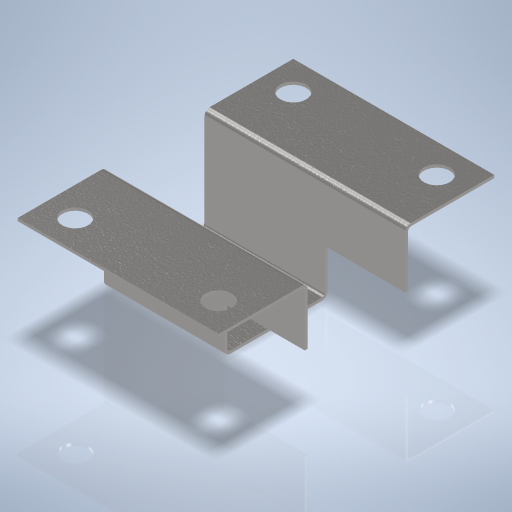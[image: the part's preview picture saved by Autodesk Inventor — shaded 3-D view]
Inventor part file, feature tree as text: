
AUTODESK INVENTOR PART (.ipt)
format: ipt  version: 2024 (Build 280153000, 153)  size: 409,600 bytes
history: native  units: mm
features: other x19, sketch x8, hole x2, projected_geometry x1
ambient origin geometry x8: Origin, YZ Plane, XZ Plane, XY Plane, X Axis, Y Axis, Z Axis, Center Point
bodies: Body1 (feature_tree)
feature tree (30):
  other  "Fläche2"
  other  "Lasche1"
  other  "Lasche2"
  other  "Lasche3"
  other  "Lasche4"
  hole  "Bohrung1"  [1 undecoded]
  hole  "Bohrung2"  [1 undecoded]
  sketch  "Skizze2"  dims[d3=2.0mm d12=18.0mm]
  other  "Grobblech2"
  sketch  "Skizze3"  dims[d13=35.0mm d14=0.5mm]
  other  "Grobblech3"
  other  "Biegung1"
  other  "Ecke1"
  sketch  "Skizze4"  dims[d15=0.5mm]
  other  "Grobblech4"
  other  "Biegung2"
  other  "Ecke2"
  sketch  "Skizze5"  dims[d16=0.25mm]
  other  "Grobblech5"
  other  "Biegung3"
  other  "Ecke3"
  sketch  "Skizze6"  dims[d17=1.0mm]
  other  "Grobblech6"
  other  "Biegung4"
  other  "Ecke4"
  sketch  "Skizze7"  dims[d18=0.5mm]
  sketch  "Skizze8"  dims[d19=18.0mm d20=90.0deg d21=0.5mm]
  projected_geometry  "Projizierte Kontur1"
  sketch  "Skizze9"  dims[d22=2.0mm d23=0.5mm d24=0.5mm d25=0.5mm d26=0.25mm d27=1.0mm d28=0.5mm d29=18.0mm d30=90.0deg d31=0.5mm d32=2.0mm d33=0.5mm d34=0.5mm d35=0.5mm d36=0.25mm d37=1.0mm d38=0.5mm d39=15.5mm d40=90.0deg d41=0.5mm d42=2.0mm d43=0.5mm d44=0.5mm d45=0.5mm d46=0.25mm d47=1.0mm d48=0.5mm d49=15.5mm d50=90.0deg d51=0.5mm d52=2.0mm d53=0.5mm d54=0.5mm d55=8.0mm d56=14.0mm d57=0.5mm d58=0.0mm d59=25.0mm d60=38.0mm d61=25.0mm d62=38.0mm d63=4.5mm d64=6.0mm d65=4.0mm d66=2.0mm d67=90.0deg d68=0.5mm d69=20.594885mm d70=8.0mm d71=8.0mm d72=3.0mm d73=6.0mm d74=4.0mm d75=2.0mm d76=90.0deg d77=8.0mm d78=20.594885mm]
  other  "Ausschneiden1"
note: 2 required parameter values undecoded (feature->parameter linkage not recoverable at this tier; creation-order binding heuristic only, values carry confidence <= 0.55)
